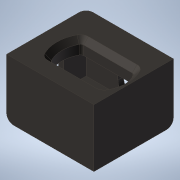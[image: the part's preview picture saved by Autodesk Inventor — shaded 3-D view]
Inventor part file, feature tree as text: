
AUTODESK INVENTOR PART (.ipt)
format: ipt  version: 2020 (Build 240168000, 168)  size: 165,888 bytes
history: mixed  units: mm
features: fillet x1, imported_body x1
ambient origin geometry x8: Origin, YZ Plane, XZ Plane, XY Plane, X Axis, Y Axis, Z Axis, Center Point
bodies: Solid1 (imported_parasolid)
feature tree (2):
  fillet  "Fillet2"  [1 undecoded]
  imported_body  NMx_Import_Brep_tag  [imported B-rep: ~18 faces, bbox_mm=[164.338, 79.502, 149.352]]
note: 1 required parameter value undecoded (feature->parameter linkage not recoverable at this tier; creation-order binding heuristic only, values carry confidence <= 0.55)
